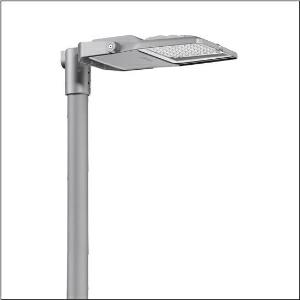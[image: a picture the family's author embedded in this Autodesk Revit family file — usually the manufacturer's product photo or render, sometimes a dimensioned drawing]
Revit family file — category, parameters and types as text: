
# Revit family: floodlight_fl_21_iq_mini___pl43_5xa7772b2a3a_a256
name_source: partatom
category: Lighting Fixtures
units: mm (PartAtom-declared; Revit-internal decimal feet)

## family parameters
Cut with Voids When Loaded = No
Host = Face
Light Source = No
Part Type = Normal
Room Calculation Point = No
Round Connector Dimension = Use Diameter
Shared = No

## types (1)
- --- (1 x LED, 6400 lm, 45.5 W, 3000K)
    Apparent Load = 46 VA
    CIE Flux Codes = 27 78 99 100 100
    Color Rendering = 70
    Color Temperature = 3000K
    Default Elevation = 1800 mm
    Description = Floodlight FL 21 iQ mini, floodlight, primary light control with lens, of PMMA, primary optical cover: protective disc, of toughened safety glass, transparent, light distribution: PL43, light emission: direct distribution, installation type: surface-mounted, LED, High Power LED, rated luminous flux: 6.400lm, luminous efficacy: 141lm/W, light colour: 730, colour temperature: 3000K, control: Auto-Match, Temp-Guard, Night-Set, Smart-Wire, Desk-Remote (wireless, voltage-free reading and setting of iQ features in the workshop via application-optimized NFC function/RFID function), optimised constant luminous flux control (CLO 2.0), Light-Fading, Lumen-Switch, with terminal, 6-pole, mains connection: 220..240V, AC, 50/60Hz, start of lifetime: 46W, end of service life: 48W, reduction: 22W, luminaire housing, of diecast aluminium, powder-coated, Siteco® metallic grey (DB 702S), corrosivity category C5 mid according to DIN EN ISO 12944, sealing non-destructively replaceable, please order mast flange separately, mast bracket, of steel, galvanised, powder-coated, protection rating (complete): IP66, insulation class (complete): insulation class II (safety insulation), certification: CE, ENEC, VDE, protection symbol: D, impact resistance: IK08, permissible operating ambient temperature: -40..+40°C, permissible operating ambient temperature for outdoor applications: -40..+50°C, standard: DIN EN 12944, LABS conformity tested according to VDMA 24364:2018-05, packaging unit: 1 piece

Light Distribution: PL43
    Height = 70 mm
    Lamp = 1 x LED
    Lamp Light Flux = 6400 lm
    Lamp Power = 45.5 W
    Lamp count = 1
    Length = 485 mm
    Luminous efficacy = 141 lm/W
    Manufacturer = Siteco
    ModVariant = No
    Model = 5XA7772B2A3A
    Number of Poles = 1
    OnlyDefault = Yes
    Power Factor = 1
    Product Name = Floodlight FL 21 iQ mini | PL43
    Product group = floodlight | pylon annexe
    ProductGroupID = 6200
    Protection Class = Protection class II
    Protection Degree = IP 66
    RLX_Detail_Level = 1
    RLX_Emergency_Light_Flux = 0 lm
    RLX_Emergency_Type = 0
    RLX_Emergency_Type_DB = No
    RlxData = <blob elided: 101005 chars, md5=8932a0a1>
    Socket = socket
    Standby Power = 0 W
    System Light Flux = 6400 lm
    System Power = 46 W
    Type Comments = factory setting: luminous flux: 100 % | dim-lin: 254 | 463 mA
    Type Image = l_1007125.jpg
    URL = http://relux.com
    VarID = @adj_112941
    Voltage = 0 V
    Weight = 0.00 kg
    Width = 337 mm

## geometry (parser evidence)
native form markers: Blend x4, Sweep x12
no freeform markers — native parametric forms only
